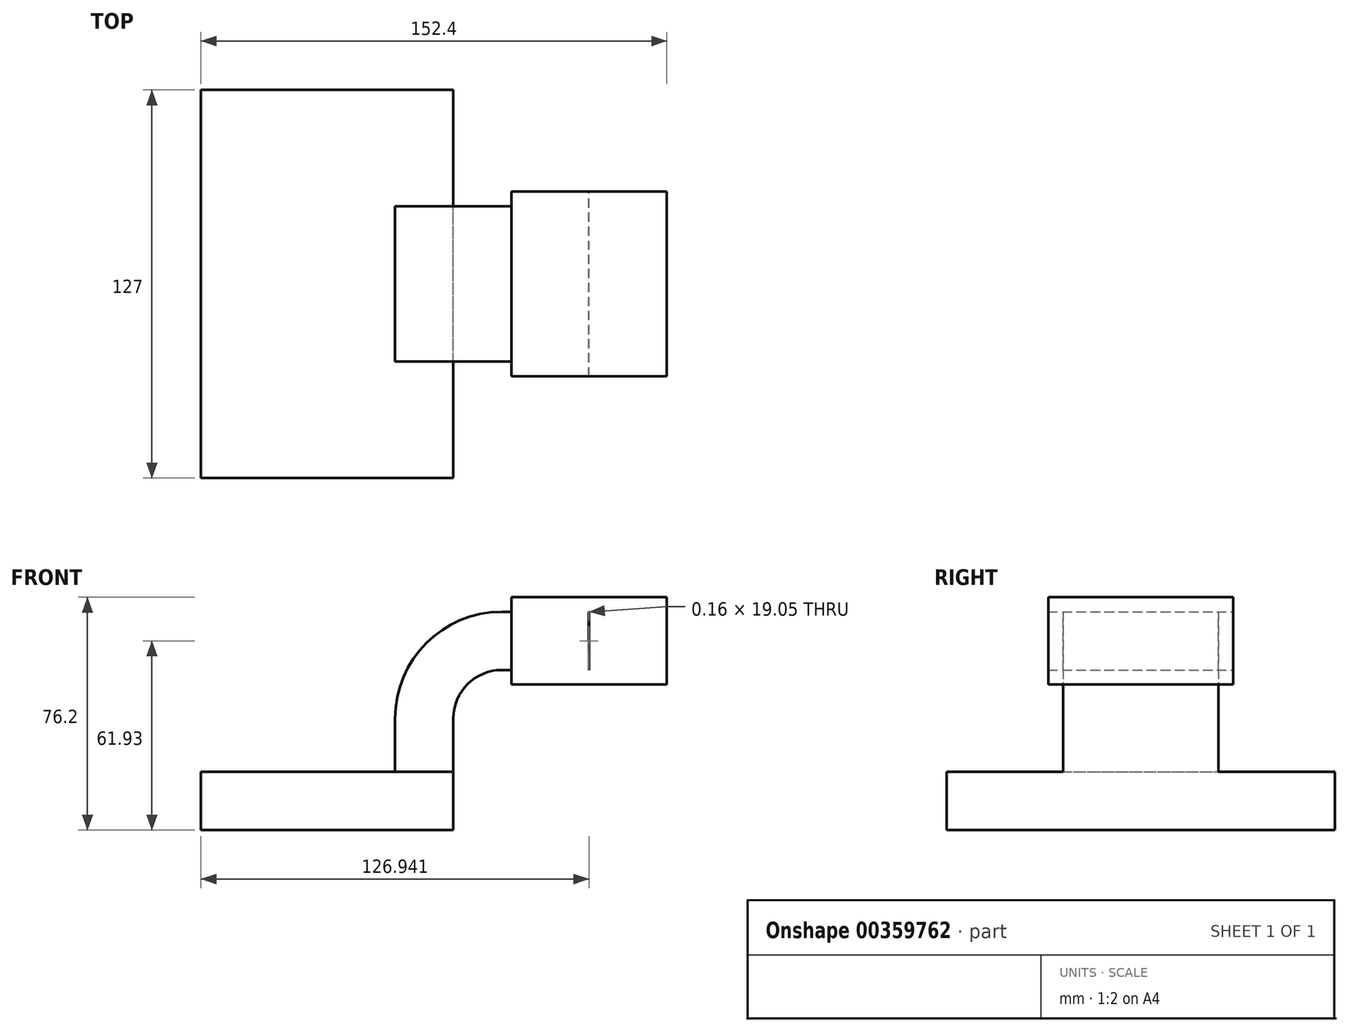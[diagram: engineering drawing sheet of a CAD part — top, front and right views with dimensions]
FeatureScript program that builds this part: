
annotation { "Feature Type Name" : "Feature", "Feature Type Description" : "" }
export const myFeature = defineFeature(function(context is Context, id is Id, definition is map)
    precondition{}
    {
        {
            var Q0;
            Q0=qCreatedBy(makeId("Front.planeOp"),FACE);
            var sketch = newSketch(context, id + "F0", { "sketchPlane" : qUnion([Q0])});
            skLineSegment(sketch, "E0.bottom", {"start": v(-41.27, -9.53) * mm, "end": v(41.28, -9.53) * mm});
            skLineSegment(sketch, "E0.top", {"start": v(-41.28, 9.53) * mm, "end": v(41.28, 9.53) * mm});
            skLineSegment(sketch, "E0.left", {"start": v(-41.28, -9.53) * mm, "end": v(-41.28, 9.53) * mm});
            skLineSegment(sketch, "E0.right", {"start": v(41.28, -9.53) * mm, "end": v(41.28, 9.52) * mm});
            skPoint(sketch, "E0.middle", {"position": v(0, 0) * mm});
            skLineSegment(sketch, "E1.bottom", {"start": v(111.12, 38.1) * mm, "end": v(60.32, 38.1) * mm});
            skLineSegment(sketch, "E1.top", {"start": v(111.12, 66.67) * mm, "end": v(60.32, 66.67) * mm});
            skLineSegment(sketch, "E1.left", {"start": v(111.12, 38.1) * mm, "end": v(111.12, 66.67) * mm});
            skLineSegment(sketch, "E1.right", {"start": v(60.32, 38.1) * mm, "end": v(60.32, 66.67) * mm});
            skPoint(sketch, "E1.middle", {"position": v(85.72, 52.39) * mm});
            skLineSegment(sketch, "E2", {"start": v(41.28, 9.52) * mm, "end": v(41.28, 27) * mm});
            skArc(sketch, "E3", {"start": v(41.27, 27) * mm, "mid": v(45.92, 38.23) * mm, "end": v(57.15, 42.88) * mm});
            skLineSegment(sketch, "E4", {"start": v(57.15, 42.88) * mm, "end": v(85.74, 42.88) * mm});
            skLineSegment(sketch, "E5.0", {"start": v(57.15, 61.93) * mm, "end": v(85.63, 61.93) * mm});
            skArc(sketch, "E5.1", {"start": v(22.22, 27) * mm, "mid": v(32.45, 51.7) * mm, "end": v(57.15, 61.93) * mm});
            skLineSegment(sketch, "E5.2", {"start": v(22.23, 9.52) * mm, "end": v(22.23, 27) * mm});
            skLineSegment(sketch, "E6", {"start": v(85.74, 42.88) * mm, "end": v(85.63, 61.93) * mm});
            skFitSpline(sketch, "E7", {"points": [v(-41.28, 9.53) * mm, v(57.15, 61.93) * mm], "startDerivative": vector(33.84, 125) * mm, "endDerivative": vector(96.92, -10.85) * mm});
            skPoint(sketch, "E8.startSnap0", {"position": v(85.72, 38.1) * mm});
            skLineSegment(sketch, "E9", {"start": v(85.72, 38.1) * mm, "end": v(85.55, 66.67) * mm});
            skSolve(sketch);
        }
        {
            var Q0;
            Q0=makeQuery(id+"F0.imprint","IMPRINT",FACE,{"disambiguationData":[TD([[makeQuery(id+"F0.imprint","IMPRINT",EDGE,{"derivedFrom":sQuery(id+"F0.wireOp",EDGE,"E0.bottom")}),1.0]])]});
            extrude(context, id + "F1", {"entities" : qUnion([Q0]), "endBound" : BoundingType.SYMMETRIC, "depth" : 127 * mm});
        }
        {
            var Q0;
            Q0=makeQuery(id+"F0.imprint","IMPRINT",FACE,{"disambiguationData":[TD([[makeQuery(id+"F0.imprint","IMPRINT",EDGE,{"derivedFrom":sQuery(id+"F0.wireOp",EDGE,"E5.1")}),1.0]])]});
            extrude(context, id + "F2", {"entities" : qUnion([Q0]), "operationType" : NewBodyOperationType.ADD, "endBound" : BoundingType.SYMMETRIC, "depth" : 15.88 * mm});
        }
        {
            var Q0;
            {var subQ0=sQuery(id+"F0.wireOp",EDGE,"E2");Q0=makeQuery(id+"F0.imprint","IMPRINT",FACE,{"disambiguationData":[TD([[makeQuery(id+"F0.imprint","IMPRINT",EDGE,{"derivedFrom":subQ0}),1.0]])]});}
            extrude(context, id + "F3", {"entities" : qUnion([Q0]), "operationType" : NewBodyOperationType.ADD, "endBound" : BoundingType.SYMMETRIC, "depth" : 50.8 * mm});
        }
        {
            var Q0;
            {var subQ0=sQuery(id+"F0.wireOp",EDGE,"E1.right");var subQ1=sQuery(id+"F0.wireOp",EDGE,"E1.bottom");var subQ2=makeQuery(id+"F0.imprint","INTERSECT",VERTEX,{"derivedFrom":[subQ1,subQ0]});Q0=makeQuery(id+"F0.imprint","IMPRINT",FACE,{"disambiguationData":[TD([[makeQuery(id+"F0.imprint","IMPRINT",EDGE,{"disambiguationData":[TD([[subQ2,1.0]])],"derivedFrom":subQ1}),-1.0]])]});}
            var Q1;
            {var subQ0=sQuery(id+"F0.wireOp",EDGE,"E1.right");var subQ1=sQuery(id+"F0.wireOp",EDGE,"E1.top");var subQ2=makeQuery(id+"F0.imprint","INTERSECT",VERTEX,{"derivedFrom":[subQ1,subQ0]});Q1=makeQuery(id+"F0.imprint","IMPRINT",FACE,{"disambiguationData":[TD([[makeQuery(id+"F0.imprint","IMPRINT",EDGE,{"disambiguationData":[TD([[subQ2,1.0]])],"derivedFrom":subQ1}),1.0]])]});}
            var Q2;
            {var subQ0=sQuery(id+"F0.wireOp",EDGE,"E4");var subQ1=sQuery(id+"F0.wireOp",EDGE,"E1.right");var subQ2=makeQuery(id+"F0.imprint","INTERSECT",VERTEX,{"derivedFrom":[subQ1,subQ0]});Q2=makeQuery(id+"F0.imprint","IMPRINT",FACE,{"disambiguationData":[TD([[makeQuery(id+"F0.imprint","IMPRINT",EDGE,{"disambiguationData":[TD([[subQ2,-1.0]])],"derivedFrom":subQ1}),-1.0]])]});}
            var Q3;
            {var subQ0=sQuery(id+"F0.wireOp",EDGE,"E1.left");Q3=makeQuery(id+"F0.imprint","IMPRINT",FACE,{"disambiguationData":[TD([[makeQuery(id+"F0.imprint","IMPRINT",EDGE,{"derivedFrom":subQ0}),1.0]])]});}
            extrude(context, id + "F4", {"entities" : qUnion([Q0, Q1, Q2, Q3]), "operationType" : NewBodyOperationType.ADD, "endBound" : BoundingType.SYMMETRIC, "depth" : 60.45 * mm});
        }
    });
